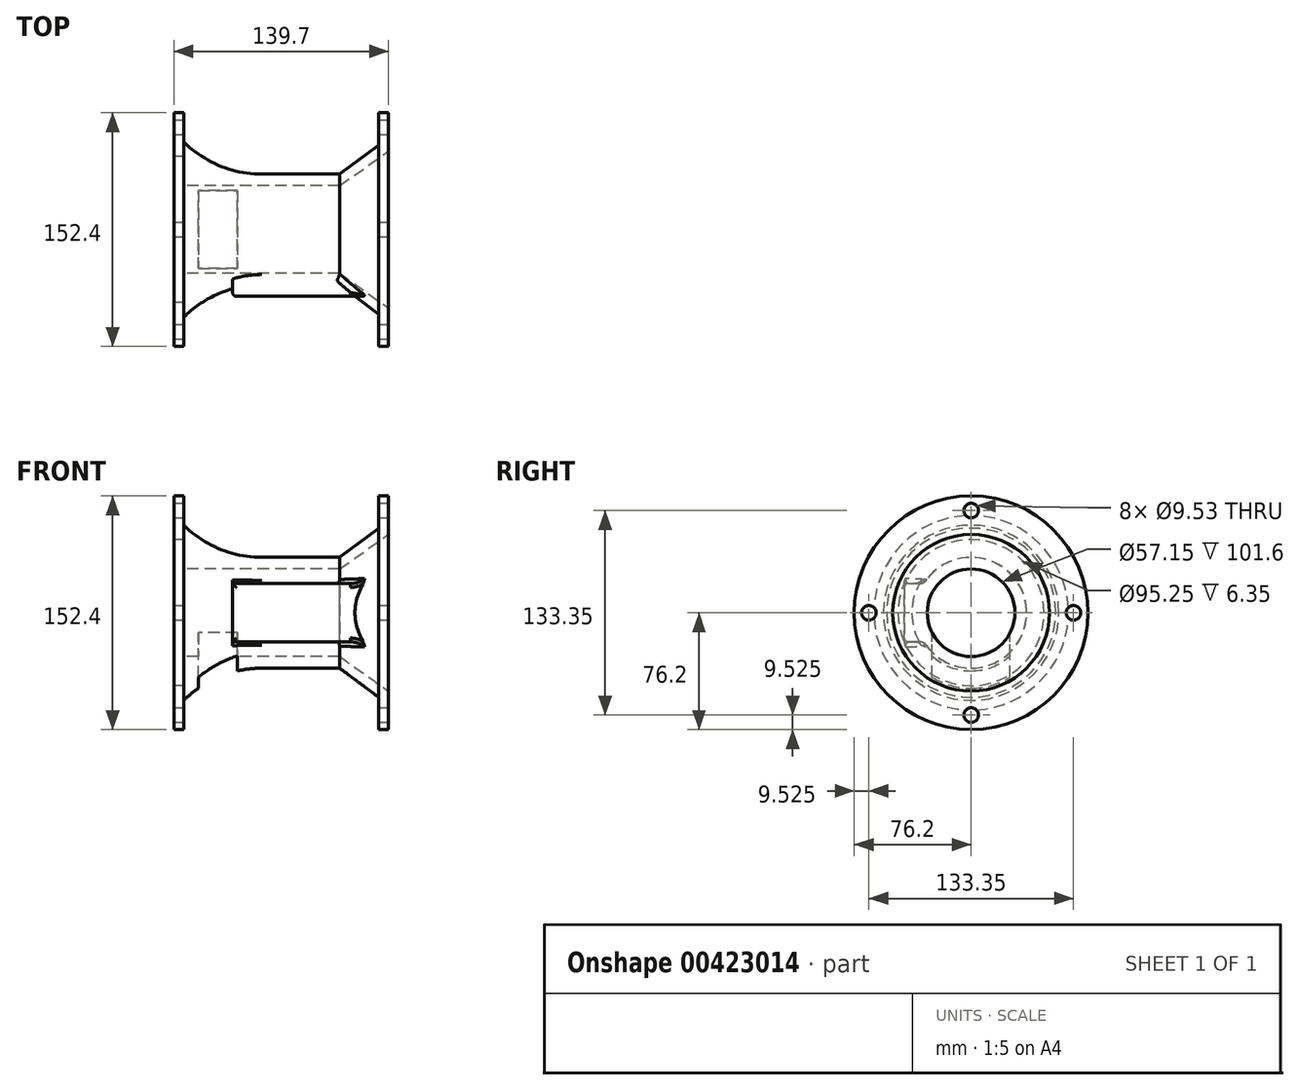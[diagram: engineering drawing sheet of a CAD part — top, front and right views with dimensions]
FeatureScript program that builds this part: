
annotation { "Feature Type Name" : "Feature", "Feature Type Description" : "" }
export const myFeature = defineFeature(function(context is Context, id is Id, definition is map)
    precondition{}
    {
        {
            var Q0;
            Q0=qCreatedBy(makeId("Right.planeOp"),FACE);
            var sketch = newSketch(context, id + "F0", { "sketchPlane" : qUnion([Q0])});
            skCircle(sketch, "E0", {"center": v(0, 0) * mm, "radius": 76.2 * mm});
            skCircle(sketch, "E1", {"center": v(0, 0) * mm, "radius": 47.63 * mm});
            skSolve(sketch);
        }
        {
            var Q0;
            Q0=makeQuery(id+"F0.imprint","IMPRINT",FACE,{"disambiguationData":[TD([[makeQuery(id+"F0.imprint","IMPRINT",EDGE,{"derivedFrom":sQuery(id+"F0.wireOp",EDGE,"E0")}),1.0]])]});
            extrude(context, id + "F1", {"entities" : qUnion([Q0]), "depth" : 6.35 * mm});
        }
        {
            var Q0;
            Q0=makeQuery(id+"F1.opExtrude","CAP_FACE",FACE,{"disambiguationData":[OSD([sQuery(id+"F0.wireOp",EDGE,"E0"),sQuery(id+"F0.wireOp",EDGE,"E1")])],"isStart":false});
            var sketch = newSketch(context, id + "F2", { "sketchPlane" : qUnion([Q0])});
            skCircle(sketch, "E2", {"center": v(0, 0) * mm, "radius": 57.15 * mm});
            skSolve(sketch);
        }
        {
            var Q0;
            Q0=makeQuery(id+"F2.imprint","IMPRINT",FACE,{"disambiguationData":[TD([[makeQuery(id+"F2.imprint","IMPRINT",EDGE,{"derivedFrom":sQuery(id+"F2.wireOp",EDGE,"E2")}),1.0]])]});
            var Q1;
            Q1=makeQuery(id+"F2.imprint","IMPRINT",FACE,{"disambiguationData":[TD([[makeQuery(id+"F2.imprint","IMPRINT",EDGE,{"derivedFrom":makeQuery(id+"F1.opExtrude","CAP_EDGE",EDGE,{"disambiguationData":[OSD([sQuery(id+"F0.wireOp",EDGE,"E1")])],"isStart":false})}),1.0]])]});
            extrude(context, id + "F3", {"entities" : qUnion([Q0, Q1]), "operationType" : NewBodyOperationType.ADD, "depth" : 127 * mm});
        }
        {
            var Q0;
            Q0=makeQuery(id+"F3.opExtrude","CAP_FACE",FACE,{"disambiguationData":[OSD([sQuery(id+"F2.wireOp",EDGE,"E2")])],"isStart":false});
            var sketch = newSketch(context, id + "F4", { "sketchPlane" : qUnion([Q0])});
            skCircle(sketch, "E3", {"center": v(0, 0) * mm, "radius": 76.2 * mm});
            skSolve(sketch);
        }
        {
            var Q0;
            Q0 = qSketchRegion(id + "F4", true);
            extrude(context, id + "F5", {"entities" : qUnion([Q0]), "operationType" : NewBodyOperationType.ADD, "depth" : 6.35 * mm});
        }
        {
            var Q0;
            Q0=makeQuery(id+"F3.opExtrude","CAP_FACE",FACE,{"disambiguationData":[OSD([sQuery(id+"F2.wireOp",EDGE,"E2")])],"isStart":true});
            var sketch = newSketch(context, id + "F6", { "sketchPlane" : qUnion([Q0])});
            skCircle(sketch, "E4", {"center": v(0, 0) * mm, "radius": 28.58 * mm});
            skSolve(sketch);
        }
        {
            var Q0;
            Q0=makeQuery(id+"F6.imprint","IMPRINT",FACE,{"disambiguationData":[TD([[makeQuery(id+"F6.imprint","IMPRINT",EDGE,{"derivedFrom":sQuery(id+"F6.wireOp",EDGE,"E4")}),1.0]])]});
            extrude(context, id + "F7", {"entities" : qUnion([Q0]), "operationType" : NewBodyOperationType.REMOVE, "oppositeDirection" : true, "depth" : 101.6 * mm});
        }
        {
            var Q0;
            Q0=makeQuery(id+"F7.boolean.opBoolean","COPY",FACE,{"derivedFrom":makeQuery(id+"F7.opExtrude","CAP_FACE",FACE,{"disambiguationData":[OSD([sQuery(id+"F6.wireOp",EDGE,"E4")])],"isStart":false})});
            var sketch = newSketch(context, id + "F8", { "sketchPlane" : qUnion([Q0])});
            skCircle(sketch, "E5", {"center": v(0, 0) * mm, "radius": 28.58 * mm});
            skSolve(sketch);
        }
        {
            var Q0;
            Q0 = qSketchRegion(id + "F8", true);
            extrude(context, id + "F9", {"entities" : qUnion([Q0]), "operationType" : NewBodyOperationType.REMOVE, "oppositeDirection" : true, "depth" : 53.97 * mm, "hasDraft" : true, "draftAngle" : 19.65 * degree});
        }
        {
            var Q0;
            Q0=qCreatedBy(makeId("Top.planeOp"),FACE);
            var sketch = newSketch(context, id + "F10", { "sketchPlane" : qUnion([Q0])});
            skLineSegment(sketch, "E6.bottom", {"start": v(41.27, 25.4) * mm, "end": v(15.88, 25.4) * mm});
            skLineSegment(sketch, "E6.top", {"start": v(41.27, -25.4) * mm, "end": v(15.87, -25.4) * mm});
            skLineSegment(sketch, "E6.left", {"start": v(41.27, 25.4) * mm, "end": v(41.27, -25.4) * mm});
            skLineSegment(sketch, "E6.right", {"start": v(15.88, 25.4) * mm, "end": v(15.87, -25.4) * mm});
            skPoint(sketch, "E6.middle", {"position": v(28.57, 0) * mm});
            skSolve(sketch);
        }
        {
            var Q0;
            Q0 = qSketchRegion(id + "F10", true);
            extrude(context, id + "F11", {"entities" : qUnion([Q0]), "operationType" : NewBodyOperationType.REMOVE, "oppositeDirection" : true, "depth" : 76.2 * mm});
        }
        {
            var Q0;
            Q0=qCreatedBy(makeId("Top.planeOp"),FACE);
            var sketch = newSketch(context, id + "F12", { "sketchPlane" : qUnion([Q0])});
            skLineSegment(sketch, "E7.bottom", {"start": v(18.63, 39.07) * mm, "end": v(6.35, 39.07) * mm});
            skLineSegment(sketch, "E7.top", {"start": v(18.63, -39.07) * mm, "end": v(6.35, -39.07) * mm});
            skLineSegment(sketch, "E7.left", {"start": v(18.63, 39.07) * mm, "end": v(18.63, -39.07) * mm});
            skLineSegment(sketch, "E7.right", {"start": v(6.35, 39.07) * mm, "end": v(6.35, -39.07) * mm});
            skPoint(sketch, "E7.middle", {"position": v(12.5, 0) * mm});
            skSolve(sketch);
        }
        {
            var Q0;
            Q0=qCreatedBy(makeId("Front.planeOp"),FACE);
            var sketch = newSketch(context, id + "F13", { "sketchPlane" : qUnion([Q0])});
            skLineSegment(sketch, "E8", {"start": v(0, 0) * mm, "end": v(154.85, 0) * mm});
            skSolve(sketch);
        }
        {
            var Q0;
            Q0=qCreatedBy(makeId("Front.planeOp"),FACE);
            var sketch = newSketch(context, id + "F14", { "sketchPlane" : qUnion([Q0])});
            skLineSegment(sketch, "E9", {"start": v(133.35, 55.13) * mm, "end": v(107.95, 36.15) * mm});
            skLineSegment(sketch, "E10", {"start": v(107.95, 36.15) * mm, "end": v(57.15, 36.15) * mm});
            skArc(sketch, "E11", {"start": v(57.15, 36.15) * mm, "mid": v(29.66, 41.6) * mm, "end": v(6.35, 57.16) * mm});
            skLineSegment(sketch, "E12", {"start": v(6.35, 57.16) * mm, "end": v(6.35, 63.39) * mm});
            skLineSegment(sketch, "E13", {"start": v(6.35, 63.39) * mm, "end": v(133.75, 63.39) * mm});
            skLineSegment(sketch, "E14", {"start": v(133.75, 63.39) * mm, "end": v(133.35, 55.13) * mm});
            skSolve(sketch);
        }
        {
            var Q0;
            Q0=qCreatedBy(makeId("Front.planeOp"),FACE);
            cPlane(context, id + "F15", {"entities" : qUnion([Q0]), "cplaneType" : CPlaneType.OFFSET, "offset" : 28.57 * mm, "width" : 152.4 * mm, "height" : 152.4 * mm});
        }
        {
            var Q0;
            Q0 = qSketchRegion(id + "F14", true);
            var Q1;
            Q1=sQuery(id+"F13.wireOp",EDGE,"E8");
            revolve(context, id + "F16", {"operationType" : NewBodyOperationType.REMOVE, "entities" : qUnion([Q0]), "axis" : qUnion([Q1]), "revolveType" : RevolveType.FULL, "oppositeDirection" : true});
        }
        {
            var Q0;
            Q0=qCreatedBy(id+"F15.planeOp",FACE);
            var sketch = newSketch(context, id + "F17", { "sketchPlane" : qUnion([Q0])});
            skLineSegment(sketch, "E15.bottom", {"start": v(127, 19.05) * mm, "end": v(38.1, 19.05) * mm});
            skLineSegment(sketch, "E15.top", {"start": v(127, -19.05) * mm, "end": v(38.1, -19.05) * mm});
            skLineSegment(sketch, "E15.left", {"start": v(127, 19.05) * mm, "end": v(127, -19.05) * mm});
            skLineSegment(sketch, "E15.right", {"start": v(38.1, 19.05) * mm, "end": v(38.1, -19.05) * mm});
            skPoint(sketch, "E15.middle", {"position": v(82.55, 0) * mm});
            skSolve(sketch);
        }
        {
            var Q0;
            Q0 = qSketchRegion(id + "F17", true);
            extrude(context, id + "F18", {"entities" : qUnion([Q0]), "operationType" : NewBodyOperationType.ADD, "depth" : 15 * mm});
        }
        {
            var Q0;
            Q0=makeQuery(id+"F18.boolean.opBoolean","INTERSECT",EDGE,{"derivedFrom":[makeQuery(id+"F16.boolean.opBoolean","COPY",FACE,{"derivedFrom":makeQuery(id+"F16.opRevolve","SWEPT_FACE",FACE,{"disambiguationData":[OSD([sQuery(id+"F14.wireOp",EDGE,"E9")])]})}),makeQuery(id+"F18.opExtrude","SWEPT_FACE",FACE,{"disambiguationData":[OSD([sQuery(id+"F17.wireOp",EDGE,"E15.bottom")])]})]});
            var Q1;
            Q1=makeQuery(id+"F18.boolean.opBoolean","INTERSECT",EDGE,{"derivedFrom":[makeQuery(id+"F16.boolean.opBoolean","COPY",FACE,{"derivedFrom":makeQuery(id+"F16.opRevolve","SWEPT_FACE",FACE,{"disambiguationData":[OSD([sQuery(id+"F14.wireOp",EDGE,"E10")])]})}),makeQuery(id+"F18.opExtrude","SWEPT_FACE",FACE,{"disambiguationData":[OSD([sQuery(id+"F17.wireOp",EDGE,"E15.bottom")])]})]});
            var Q2;
            Q2=makeQuery(id+"F18.boolean.opBoolean","INTERSECT",EDGE,{"derivedFrom":[makeQuery(id+"F16.boolean.opBoolean","COPY",FACE,{"derivedFrom":makeQuery(id+"F16.opRevolve","SWEPT_FACE",FACE,{"disambiguationData":[OSD([sQuery(id+"F14.wireOp",EDGE,"E10")])]})}),makeQuery(id+"F18.opExtrude","SWEPT_FACE",FACE,{"disambiguationData":[OSD([sQuery(id+"F17.wireOp",EDGE,"E15.top")])]})]});
            var Q3;
            Q3=makeQuery(id+"F18.boolean.opBoolean","INTERSECT",EDGE,{"derivedFrom":[makeQuery(id+"F16.boolean.opBoolean","COPY",FACE,{"derivedFrom":makeQuery(id+"F16.opRevolve","SWEPT_FACE",FACE,{"disambiguationData":[OSD([sQuery(id+"F14.wireOp",EDGE,"E9")])]})}),makeQuery(id+"F18.opExtrude","SWEPT_FACE",FACE,{"disambiguationData":[OSD([sQuery(id+"F17.wireOp",EDGE,"E15.top")])]})]});
            var Q4;
            Q4=makeQuery(id+"F18.boolean.opBoolean","INTERSECT",EDGE,{"derivedFrom":[makeQuery(id+"F16.boolean.opBoolean","COPY",FACE,{"derivedFrom":makeQuery(id+"F16.opRevolve","SWEPT_FACE",FACE,{"disambiguationData":[OSD([sQuery(id+"F14.wireOp",EDGE,"E10")])]})}),makeQuery(id+"F18.opExtrude","SWEPT_FACE",FACE,{"disambiguationData":[OSD([sQuery(id+"F17.wireOp",EDGE,"E15.right")])]})]});
            fillet(context, id + "F19", {"entities" : qUnion([Q0, Q1, Q2, Q3, Q4]), "radius" : 5.08 * mm, "tangentPropagation" : true, "allowEdgeOverflow" : false});
        }
        {
            var Q0;
            Q0=qCreatedBy(makeId("Top.planeOp"),FACE);
            var sketch = newSketch(context, id + "F20", { "sketchPlane" : qUnion([Q0])});
            skLineSegment(sketch, "E16", {"start": v(107.95, 28.58) * mm, "end": v(140.17, 51.4) * mm});
            skLineSegment(sketch, "E17", {"start": v(107.95, 28.58) * mm, "end": v(107.95, 0) * mm});
            skLineSegment(sketch, "E18", {"start": v(140.17, 51.4) * mm, "end": v(140.17, 0) * mm});
            skLineSegment(sketch, "E19", {"start": v(140.17, 0) * mm, "end": v(107.95, 0) * mm});
            skSolve(sketch);
        }
        {
            var Q0;
            Q0=qCreatedBy(makeId("Top.planeOp"),FACE);
            var sketch = newSketch(context, id + "F21", { "sketchPlane" : qUnion([Q0])});
            skLineSegment(sketch, "E20", {"start": v(-10.63, 0) * mm, "end": v(161.7, 0) * mm});
            skSolve(sketch);
        }
        {
            var Q0;
            Q0 = qSketchRegion(id + "F20", true);
            var Q1;
            Q1=sQuery(id+"F21.wireOp",EDGE,"E20");
            revolve(context, id + "F22", {"operationType" : NewBodyOperationType.REMOVE, "entities" : qUnion([Q0]), "axis" : qUnion([Q1]), "revolveType" : RevolveType.FULL, "oppositeDirection" : true});
        }
        {
            var Q0;
            Q0=makeQuery(id+"F18.opExtrude","CAP_EDGE",EDGE,{"disambiguationData":[OSD([sQuery(id+"F17.wireOp",EDGE,"E15.top")])],"isStart":false});
            var Q1;
            Q1=makeQuery(id+"F18.opExtrude","CAP_EDGE",EDGE,{"disambiguationData":[OSD([sQuery(id+"F17.wireOp",EDGE,"E15.right")])],"isStart":false});
            var Q2;
            Q2=makeQuery(id+"F18.opExtrude","CAP_EDGE",EDGE,{"disambiguationData":[OSD([sQuery(id+"F17.wireOp",EDGE,"E15.bottom")])],"isStart":false});
            fillet(context, id + "F23", {"entities" : qUnion([Q0, Q1, Q2]), "radius" : 2.54 * mm, "tangentPropagation" : true, "allowEdgeOverflow" : false});
        }
        {
            var Q0;
            Q0=makeQuery(id+"F5.opExtrude","CAP_FACE",FACE,{"disambiguationData":[OSD([sQuery(id+"F4.wireOp",EDGE,"E3")])],"isStart":false});
            var sketch = newSketch(context, id + "F24", { "sketchPlane" : qUnion([Q0])});
            skPoint(sketch, "E21", {"position": v(0, 66.67) * mm});
            skPoint(sketch, "E22", {"position": v(66.68, 0) * mm});
            skPoint(sketch, "E23", {"position": v(0, -66.68) * mm});
            skPoint(sketch, "E24", {"position": v(-66.68, 0) * mm});
            skSolve(sketch);
        }
        {
            var Q0;
            Q0=sQuery(id+"F24.wireOp",VERTEX,"E24");
            var Q1;
            Q1=sQuery(id+"F24.wireOp",VERTEX,"E21");
            var Q2;
            Q2=sQuery(id+"F24.wireOp",VERTEX,"E22");
            var Q3;
            Q3=sQuery(id+"F24.wireOp",VERTEX,"E23");
            var Q4;
            Q4=makeQuery(id+"F1.opExtrude","SWEPT_BODY",BODY,{"disambiguationData":[OSD([sQuery(id+"F0.wireOp",EDGE,"E0"),sQuery(id+"F0.wireOp",EDGE,"E1")])]});
            hole(context, id + "F25", {"style" : HoleStyle.C_BORE, "endStyle" : HoleEndStyle.THROUGH, "holeDiameter" : 9.52 * mm, "cBoreDiameter" : 9.52 * mm, "cBoreDepth" : 6.35 * mm, "isTappedThrough" : true, "tappedDepth" : 12.7 * mm, "tapClearance" : 3, "locations" : qUnion([Q0, Q1, Q2, Q3]), "scope" : qUnion([Q4])});
        }
    });
